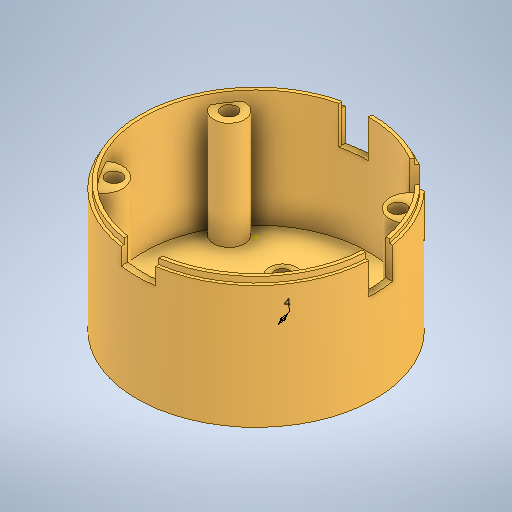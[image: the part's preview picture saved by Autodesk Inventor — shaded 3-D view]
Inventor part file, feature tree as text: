
AUTODESK INVENTOR PART (.ipt)
format: ipt  version: 2025.2 (Build 292293000, 293)  size: 554,496 bytes
history: native  units: in
note: dims shown in document units (in); Inventor stores cm internally (conversion verified against a paired STEP export)
features: sketch x13, extrude x10, other x9, direct_edit x4, move_body x3, sweep x1
ambient origin geometry x8: Origin, YZ Plane, XZ Plane, XY Plane, X Axis, Y Axis, Z Axis, Center Point
bodies: Solid1 (feature_tree), Solid2 (feature_tree), Solid3 (feature_tree)
feature tree (40):
  direct_edit  "Direct Edit1"
  sketch  "Sketch1"  dims[d0=0.1575in d1=0.0in d2=0.8268in d3=0.0in]
  direct_edit  "Direct Edit2"
  extrude  "Extrusion1"  Depth=0.8268in TaperAngle=0.0deg
  extrude  "Extrusion2"  Depth=0.748in TaperAngle=0.0deg
  extrude  "Extrusion3"  Depth=0.748in TaperAngle=0.0deg
  extrude  "Extrusion4"  Depth=0.6693in TaperAngle=0.0deg
  extrude  "Extrusion5"  Depth=0.5625in
  sweep  "Sweep1"
  direct_edit  "Direct Edit4"
  extrude  "Extrusion6"  Depth=1.9685in TaperAngle=0.0deg
  direct_edit  "Direct Edit5"
  extrude  "Extrusion7"  TaperAngle=0.0deg  [1 undecoded]
  extrude  "Extrusion8"  Depth=0.3937in TaperAngle=0.0deg
  extrude  "Extrusion9"  [1 undecoded]
  extrude  "Extrusion10"  [1 undecoded]
  sketch  "Sketch2"  dims[d4=0.1575in d5=0.748in d6=0.0in]
  sketch  "Sketch3"  dims[d7=0.315in d8=0.748in d9=0.0in]
  sketch  "Sketch4"  dims[d10=0.1575in d11=0.6693in d12=0.0in]
  sketch  "Sketch5"  dims[d13=0.0in d14=0.0in d15=0.5625in]
  sketch  "Sketch6"  dims[d16=0.0812in d17=0.0in d18=0.0in d19=0.0in d20=0.3937in]
  sketch  "Sketch7"  dims[d21=1.9685in d22=0.0in d23=1.9685in d24=0.0in]
  sketch  "3D Sketch1"
  sketch  "Sketch9"  dims[d25=0.0in d26=0.0in d27=-0.1575in d28=0.0in d29=0.0in d30=-0.1575in]
  sketch  "Sketch10"  dims[d31=0.2087in d32=0.3937in d33=0.0in]
  sketch  "Sketch11"  dims[d34=0.3937in d35=0.0in]
  sketch  "Sketch12"
  sketch  "Sketch13"
  other  "Com_Bottom_A"
  other  "Com_Bottom_B"
  other  "Com_Bottom_C"
  other  "Delete1"
  other  "Delete2"
  other  "Delete3"
  other  "Delete4"
  other  "Delete5"
  other  "Size1"
  move_body  "Move1"
  move_body  "Move2"
  move_body  "Move3"
note: 3 required parameter values undecoded (feature->parameter linkage not recoverable at this tier; creation-order binding heuristic only, values carry confidence <= 0.55)
